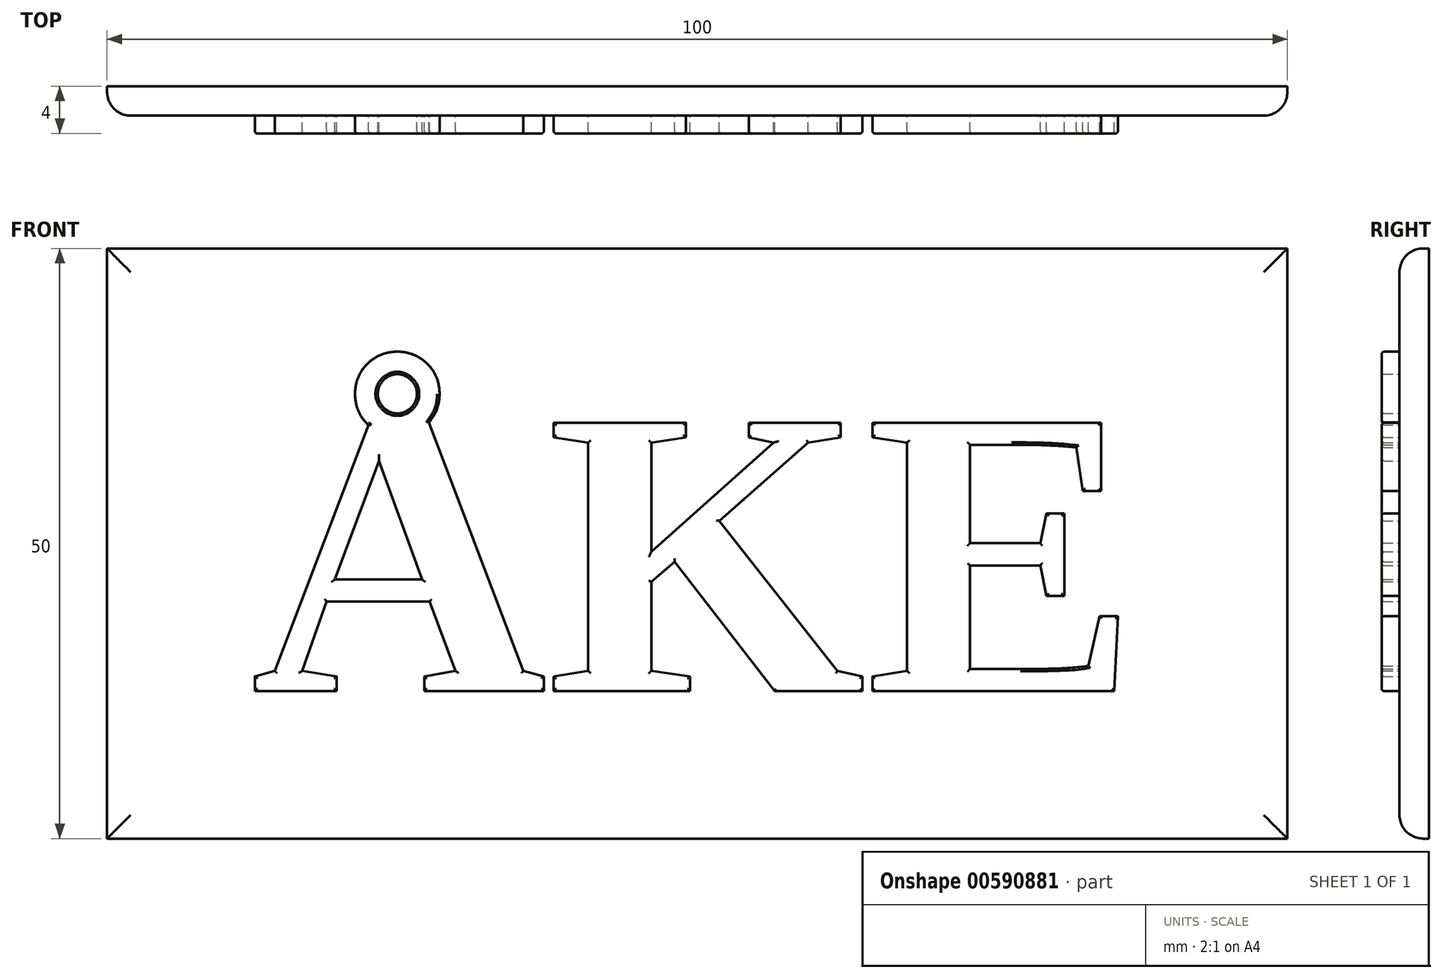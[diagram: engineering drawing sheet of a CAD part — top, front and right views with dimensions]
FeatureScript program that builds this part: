
annotation { "Feature Type Name" : "Feature", "Feature Type Description" : "" }
export const myFeature = defineFeature(function(context is Context, id is Id, definition is map)
    precondition{}
    {
        {
            var Q0;
            Q0=qCreatedBy(makeId("Front.planeOp"),FACE);
            var sketch = newSketch(context, id + "F0", { "sketchPlane" : qUnion([Q0])});
            skLineSegment(sketch, "E0.bottom", {"start": v(0, 0) * mm, "end": v(100, 0) * mm});
            skLineSegment(sketch, "E0.top", {"start": v(0, 50) * mm, "end": v(100, 50) * mm});
            skLineSegment(sketch, "E0.left", {"start": v(0, 0) * mm, "end": v(0, 50) * mm});
            skLineSegment(sketch, "E0.right", {"start": v(100, 0) * mm, "end": v(100, 50) * mm});
            skSolve(sketch);
        }
        {
            var Q0;
            Q0 = qSketchRegion(id + "F0", true);
            extrude(context, id + "F1", {"entities" : qUnion([Q0]), "depth" : 2.5 * mm, "offsetDistance" : 25 * mm});
        }
        {
            var Q0;
            Q0=makeQuery(id+"F1.opExtrude","CAP_FACE",FACE,{"disambiguationData":[OSD([sQuery(id+"F0.wireOp",EDGE,"E0.bottom"),sQuery(id+"F0.wireOp",EDGE,"E0.top"),sQuery(id+"F0.wireOp",EDGE,"E0.left"),sQuery(id+"F0.wireOp",EDGE,"E0.right")])],"isStart":false});
            var sketch = newSketch(context, id + "F2", { "sketchPlane" : qUnion([Q0])});
            skText(sketch, "E1", { "text": "ÅKE", "fontName": "Tinos-Bold.ttf"});
            skLineSegment(sketch, "E2", {"start": v(50, 50) * mm, "end": v(50, 0) * mm, "construction": true});
            skLineSegment(sketch, "E3", {"start": v(0, 25) * mm, "end": v(100, 25) * mm, "construction": true});
            skLineSegment(sketch, "E4", {"start": v(12.18, 25) * mm, "end": v(87.82, 25) * mm, "construction": true});
            const initialGuessF2  = {"E1": [0.01218, 0.0125, 1, 0, 0.025]};
            skSetInitialGuess(sketch, initialGuessF2);
            skSolve(sketch);
        }
        {
            var Q0;
            Q0 = qSketchRegion(id + "F2", true);
            extrude(context, id + "F3", {"entities" : qUnion([Q0]), "operationType" : NewBodyOperationType.ADD, "depth" : 1.5 * mm, "offsetDistance" : 25 * mm});
        }
        {
            var Q0;
            Q0=makeQuery(id+"F1.opExtrude","CAP_EDGE",EDGE,{"disambiguationData":[OSD([sQuery(id+"F0.wireOp",EDGE,"E0.left")])],"isStart":false});
            var Q1;
            Q1=makeQuery(id+"F1.opExtrude","CAP_EDGE",EDGE,{"disambiguationData":[OSD([sQuery(id+"F0.wireOp",EDGE,"E0.right")])],"isStart":false});
            var Q2;
            Q2=makeQuery(id+"F1.opExtrude","CAP_EDGE",EDGE,{"disambiguationData":[OSD([sQuery(id+"F0.wireOp",EDGE,"E0.bottom")])],"isStart":false});
            var Q3;
            Q3=makeQuery(id+"F1.opExtrude","CAP_EDGE",EDGE,{"disambiguationData":[OSD([sQuery(id+"F0.wireOp",EDGE,"E0.top")])],"isStart":false});
            fillet(context, id + "F4", {"entities" : qUnion([Q0, Q1, Q2, Q3]), "radius" : 2 * mm, "tangentPropagation" : true, "allowEdgeOverflow" : false});
        }
        {
            var Q0;
            Q0=makeQuery(id+"F3.opExtrude","CAP_EDGE",EDGE,{"disambiguationData":[OSD([sQuery(id+"F2.wireOp",EDGE,"E1.sketch_text.stroke-6")])],"isStart":false});
            var Q1;
            Q1=makeQuery(id+"F3.opExtrude","CAP_EDGE",EDGE,{"disambiguationData":[OSD([sQuery(id+"F2.wireOp",EDGE,"E1.sketch_text.stroke-25")])],"isStart":false});
            var Q2;
            Q2=makeQuery(id+"F3.opExtrude","CAP_EDGE",EDGE,{"disambiguationData":[OSD([sQuery(id+"F2.wireOp",EDGE,"E1.sketch_text.stroke-24")])],"isStart":false});
            var Q3;
            Q3=makeQuery(id+"F3.opExtrude","CAP_FACE",FACE,{"disambiguationData":[OSD([sQuery(id+"F2.wireOp",EDGE,"E1.sketch_text.stroke-0"),sQuery(id+"F2.wireOp",EDGE,"E1.sketch_text.stroke-1"),sQuery(id+"F2.wireOp",EDGE,"E1.sketch_text.stroke-2"),sQuery(id+"F2.wireOp",EDGE,"E1.sketch_text.stroke-3"),sQuery(id+"F2.wireOp",EDGE,"E1.sketch_text.stroke-4"),sQuery(id+"F2.wireOp",EDGE,"E1.sketch_text.stroke-6"),sQuery(id+"F2.wireOp",EDGE,"E1.sketch_text.stroke-7"),sQuery(id+"F2.wireOp",EDGE,"E1.sketch_text.stroke-8"),sQuery(id+"F2.wireOp",EDGE,"E1.sketch_text.stroke-9"),sQuery(id+"F2.wireOp",EDGE,"E1.sketch_text.stroke-10"),sQuery(id+"F2.wireOp",EDGE,"E1.sketch_text.stroke-11"),sQuery(id+"F2.wireOp",EDGE,"E1.sketch_text.stroke-12"),sQuery(id+"F2.wireOp",EDGE,"E1.sketch_text.stroke-13"),sQuery(id+"F2.wireOp",EDGE,"E1.sketch_text.stroke-14"),sQuery(id+"F2.wireOp",EDGE,"E1.sketch_text.stroke-15"),sQuery(id+"F2.wireOp",EDGE,"E1.sketch_text.stroke-16"),sQuery(id+"F2.wireOp",EDGE,"E1.sketch_text.stroke-17"),sQuery(id+"F2.wireOp",EDGE,"E1.sketch_text.stroke-18"),sQuery(id+"F2.wireOp",EDGE,"E1.sketch_text.stroke-19"),sQuery(id+"F2.wireOp",EDGE,"E1.sketch_text.stroke-20"),sQuery(id+"F2.wireOp",EDGE,"E1.sketch_text.stroke-21"),sQuery(id+"F2.wireOp",EDGE,"E1.sketch_text.stroke-22"),sQuery(id+"F2.wireOp",EDGE,"E1.sketch_text.stroke-23"),sQuery(id+"F2.wireOp",EDGE,"E1.sketch_text.stroke-24"),sQuery(id+"F2.wireOp",EDGE,"E1.sketch_text.stroke-25"),sQuery(id+"F2.wireOp",EDGE,"E1.sketch_text.stroke-27"),sQuery(id+"F2.wireOp",EDGE,"E1.sketch_text.stroke-28"),sQuery(id+"F2.wireOp",EDGE,"E1.sketch_text.stroke-29"),sQuery(id+"F2.wireOp",EDGE,"E1.sketch_text.stroke-30"),sQuery(id+"F2.wireOp",EDGE,"E1.sketch_text.stroke-31"),sQuery(id+"F2.wireOp",EDGE,"E1.sketch_text.stroke-32"),sQuery(id+"F2.wireOp",EDGE,"E1.sketch_text.stroke-33"),sQuery(id+"F2.wireOp",EDGE,"E1.sketch_text.stroke-34")])],"isStart":false});
            var Q4;
            Q4=makeQuery(id+"F3.opExtrude","CAP_FACE",FACE,{"disambiguationData":[OSD([sQuery(id+"F2.wireOp",EDGE,"E1.sketch_text.stroke-35"),sQuery(id+"F2.wireOp",EDGE,"E1.sketch_text.stroke-36"),sQuery(id+"F2.wireOp",EDGE,"E1.sketch_text.stroke-37"),sQuery(id+"F2.wireOp",EDGE,"E1.sketch_text.stroke-38"),sQuery(id+"F2.wireOp",EDGE,"E1.sketch_text.stroke-39"),sQuery(id+"F2.wireOp",EDGE,"E1.sketch_text.stroke-40"),sQuery(id+"F2.wireOp",EDGE,"E1.sketch_text.stroke-41"),sQuery(id+"F2.wireOp",EDGE,"E1.sketch_text.stroke-42"),sQuery(id+"F2.wireOp",EDGE,"E1.sketch_text.stroke-43"),sQuery(id+"F2.wireOp",EDGE,"E1.sketch_text.stroke-44"),sQuery(id+"F2.wireOp",EDGE,"E1.sketch_text.stroke-45"),sQuery(id+"F2.wireOp",EDGE,"E1.sketch_text.stroke-46"),sQuery(id+"F2.wireOp",EDGE,"E1.sketch_text.stroke-47"),sQuery(id+"F2.wireOp",EDGE,"E1.sketch_text.stroke-48"),sQuery(id+"F2.wireOp",EDGE,"E1.sketch_text.stroke-49"),sQuery(id+"F2.wireOp",EDGE,"E1.sketch_text.stroke-50"),sQuery(id+"F2.wireOp",EDGE,"E1.sketch_text.stroke-51"),sQuery(id+"F2.wireOp",EDGE,"E1.sketch_text.stroke-52"),sQuery(id+"F2.wireOp",EDGE,"E1.sketch_text.stroke-53"),sQuery(id+"F2.wireOp",EDGE,"E1.sketch_text.stroke-54"),sQuery(id+"F2.wireOp",EDGE,"E1.sketch_text.stroke-55"),sQuery(id+"F2.wireOp",EDGE,"E1.sketch_text.stroke-56"),sQuery(id+"F2.wireOp",EDGE,"E1.sketch_text.stroke-57"),sQuery(id+"F2.wireOp",EDGE,"E1.sketch_text.stroke-58"),sQuery(id+"F2.wireOp",EDGE,"E1.sketch_text.stroke-59"),sQuery(id+"F2.wireOp",EDGE,"E1.sketch_text.stroke-60")])],"isStart":false});
            var Q5;
            Q5=makeQuery(id+"F3.opExtrude","CAP_FACE",FACE,{"disambiguationData":[OSD([sQuery(id+"F2.wireOp",EDGE,"E1.sketch_text.stroke-61"),sQuery(id+"F2.wireOp",EDGE,"E1.sketch_text.stroke-62"),sQuery(id+"F2.wireOp",EDGE,"E1.sketch_text.stroke-63"),sQuery(id+"F2.wireOp",EDGE,"E1.sketch_text.stroke-64"),sQuery(id+"F2.wireOp",EDGE,"E1.sketch_text.stroke-65"),sQuery(id+"F2.wireOp",EDGE,"E1.sketch_text.stroke-66"),sQuery(id+"F2.wireOp",EDGE,"E1.sketch_text.stroke-67"),sQuery(id+"F2.wireOp",EDGE,"E1.sketch_text.stroke-68"),sQuery(id+"F2.wireOp",EDGE,"E1.sketch_text.stroke-69"),sQuery(id+"F2.wireOp",EDGE,"E1.sketch_text.stroke-70"),sQuery(id+"F2.wireOp",EDGE,"E1.sketch_text.stroke-71"),sQuery(id+"F2.wireOp",EDGE,"E1.sketch_text.stroke-72"),sQuery(id+"F2.wireOp",EDGE,"E1.sketch_text.stroke-73"),sQuery(id+"F2.wireOp",EDGE,"E1.sketch_text.stroke-74"),sQuery(id+"F2.wireOp",EDGE,"E1.sketch_text.stroke-75"),sQuery(id+"F2.wireOp",EDGE,"E1.sketch_text.stroke-76"),sQuery(id+"F2.wireOp",EDGE,"E1.sketch_text.stroke-77"),sQuery(id+"F2.wireOp",EDGE,"E1.sketch_text.stroke-78"),sQuery(id+"F2.wireOp",EDGE,"E1.sketch_text.stroke-79"),sQuery(id+"F2.wireOp",EDGE,"E1.sketch_text.stroke-80"),sQuery(id+"F2.wireOp",EDGE,"E1.sketch_text.stroke-81"),sQuery(id+"F2.wireOp",EDGE,"E1.sketch_text.stroke-82"),sQuery(id+"F2.wireOp",EDGE,"E1.sketch_text.stroke-83"),sQuery(id+"F2.wireOp",EDGE,"E1.sketch_text.stroke-84"),sQuery(id+"F2.wireOp",EDGE,"E1.sketch_text.stroke-85"),sQuery(id+"F2.wireOp",EDGE,"E1.sketch_text.stroke-86")])],"isStart":false});
            fillet(context, id + "F5", {"entities" : qUnion([Q0, Q1, Q2, Q3, Q4, Q5]), "radius" : 0.2 * mm, "tangentPropagation" : true, "allowEdgeOverflow" : false});
        }
    });
